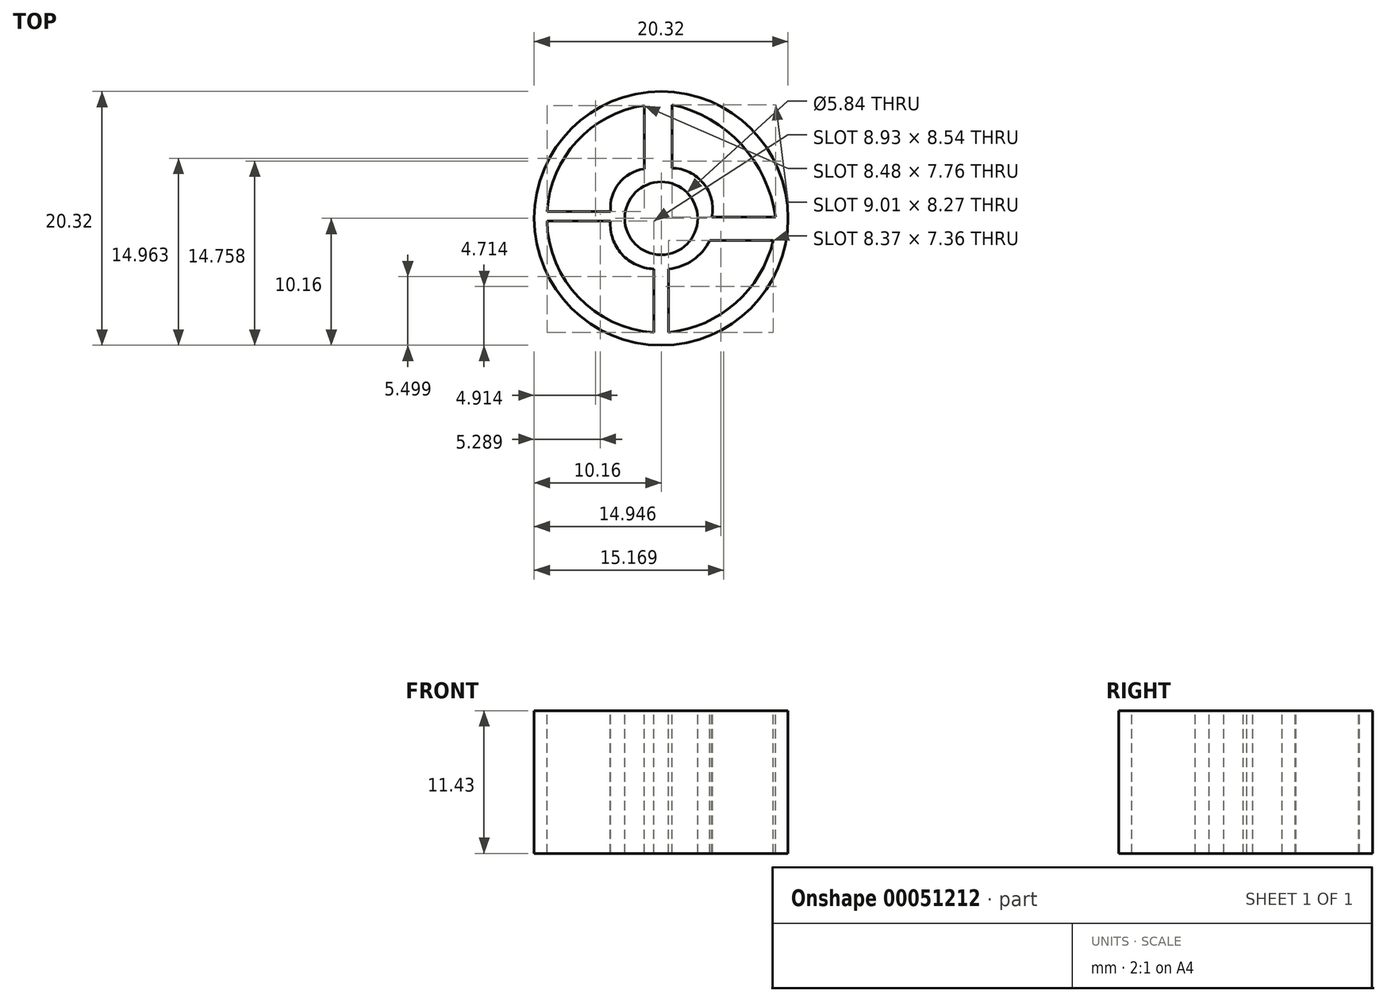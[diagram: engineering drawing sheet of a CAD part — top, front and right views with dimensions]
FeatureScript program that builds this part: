
annotation { "Feature Type Name" : "Feature", "Feature Type Description" : "" }
export const myFeature = defineFeature(function(context is Context, id is Id, definition is map)
    precondition{}
    {
        {
            var Q0;
            Q0=qCreatedBy(makeId("Top.planeOp"),FACE);
            var sketch = newSketch(context, id + "F0", { "sketchPlane" : qUnion([Q0])});
            skCircle(sketch, "E0", {"center": v(0, 0) * mm, "radius": 10.16 * mm});
            skSolve(sketch);
        }
        {
            var Q0;
            Q0=qSketchRegion(id+"F0",true);
            extrude(context, id + "F1", {"entities" : qUnion([Q0]), "depth" : 11.43 * mm});
        }
        {
            var Q0;
            Q0=makeQuery(id+"F1.opExtrude","CAP_FACE",FACE,{"disambiguationData":[OSD([sQuery(id+"F0.wireOp",EDGE,"E0")])],"isStart":false});
            var sketch = newSketch(context, id + "F2", { "sketchPlane" : qUnion([Q0])});
            skCircle(sketch, "E1", {"center": v(0, 0) * mm, "radius": 2.92 * mm});
            skSolve(sketch);
        }
        {
            var Q0;
            Q0=qSketchRegion(id+"F2",true);
            extrude(context, id + "F3", {"entities" : qUnion([Q0]), "operationType" : NewBodyOperationType.REMOVE, "oppositeDirection" : true, "depth" : 25.4 * mm});
        }
        {
            var Q0;
            Q0=makeQuery(id+"F1.opExtrude","CAP_FACE",FACE,{"disambiguationData":[OSD([sQuery(id+"F0.wireOp",EDGE,"E0")])],"isStart":false});
            var sketch = newSketch(context, id + "F4", { "sketchPlane" : qUnion([Q0])});
            skLineSegment(sketch, "E2", {"start": v(-0.6, -4.04) * mm, "end": v(-0.6, -9.12) * mm});
            skLineSegment(sketch, "E3", {"start": v(-4.06, -0.2) * mm, "end": v(-9.14, -0.2) * mm});
            skArc(sketch, "E4", {"start": v(-4.06, -0.2) * mm, "mid": v(-3.15, -2.86) * mm, "end": v(-0.6, -4.04) * mm});
            skArc(sketch, "E5", {"start": v(-9.14, -0.2) * mm, "mid": v(-6.6, -6.32) * mm, "end": v(-0.6, -9.12) * mm});
            skSolve(sketch);
        }
        {
            var Q0;
            Q0 = qSketchRegion(id + "F4", true);
            extrude(context, id + "F5", {"entities" : qUnion([Q0]), "operationType" : NewBodyOperationType.REMOVE, "oppositeDirection" : true, "depth" : 25.4 * mm});
        }
        {
            var Q0;
            Q0=makeQuery(id+"F1.opExtrude","CAP_FACE",FACE,{"disambiguationData":[OSD([sQuery(id+"F0.wireOp",EDGE,"E0")])],"isStart":false});
            var sketch = newSketch(context, id + "F6", { "sketchPlane" : qUnion([Q0])});
            skLineSegment(sketch, "E6", {"start": v(0.6, -4.04) * mm, "end": v(0.6, -9.12) * mm});
            skLineSegment(sketch, "E7", {"start": v(3.9, -1.77) * mm, "end": v(8.97, -1.77) * mm});
            skLineSegment(sketch, "E8", {"start": v(4.06, 0.1) * mm, "end": v(9.14, 0.1) * mm});
            skLineSegment(sketch, "E9", {"start": v(-1.37, 3.96) * mm, "end": v(-1.37, 9.04) * mm});
            skLineSegment(sketch, "E10", {"start": v(0.87, 4.02) * mm, "end": v(0.87, 9.1) * mm});
            skLineSegment(sketch, "E11", {"start": v(-4.05, 0.56) * mm, "end": v(-9.13, 0.56) * mm});
            skArc(sketch, "E12", {"start": v(-1.37, 3.96) * mm, "mid": v(-3.39, 2.8) * mm, "end": v(-4.05, 0.56) * mm});
            skArc(sketch, "E13", {"start": v(-1.37, 9.04) * mm, "mid": v(-6.75, 6.18) * mm, "end": v(-9.13, 0.56) * mm});
            skArc(sketch, "E14", {"start": v(4.06, 0.1) * mm, "mid": v(3.39, 2.8) * mm, "end": v(0.87, 4.02) * mm});
            skArc(sketch, "E15", {"start": v(9.14, 0.1) * mm, "mid": v(6.43, 5.9) * mm, "end": v(0.87, 9.1) * mm});
            skArc(sketch, "E16", {"start": v(0.6, -4.04) * mm, "mid": v(2.54, -3.33) * mm, "end": v(3.9, -1.77) * mm});
            skArc(sketch, "E17", {"start": v(0.6, -9.12) * mm, "mid": v(5.96, -6.78) * mm, "end": v(8.97, -1.77) * mm});
            skSolve(sketch);
        }
        {
            var Q0;
            Q0 = qSketchRegion(id + "F6", true);
            extrude(context, id + "F7", {"entities" : qUnion([Q0]), "operationType" : NewBodyOperationType.REMOVE, "oppositeDirection" : true, "depth" : 25.4 * mm});
        }
    });
